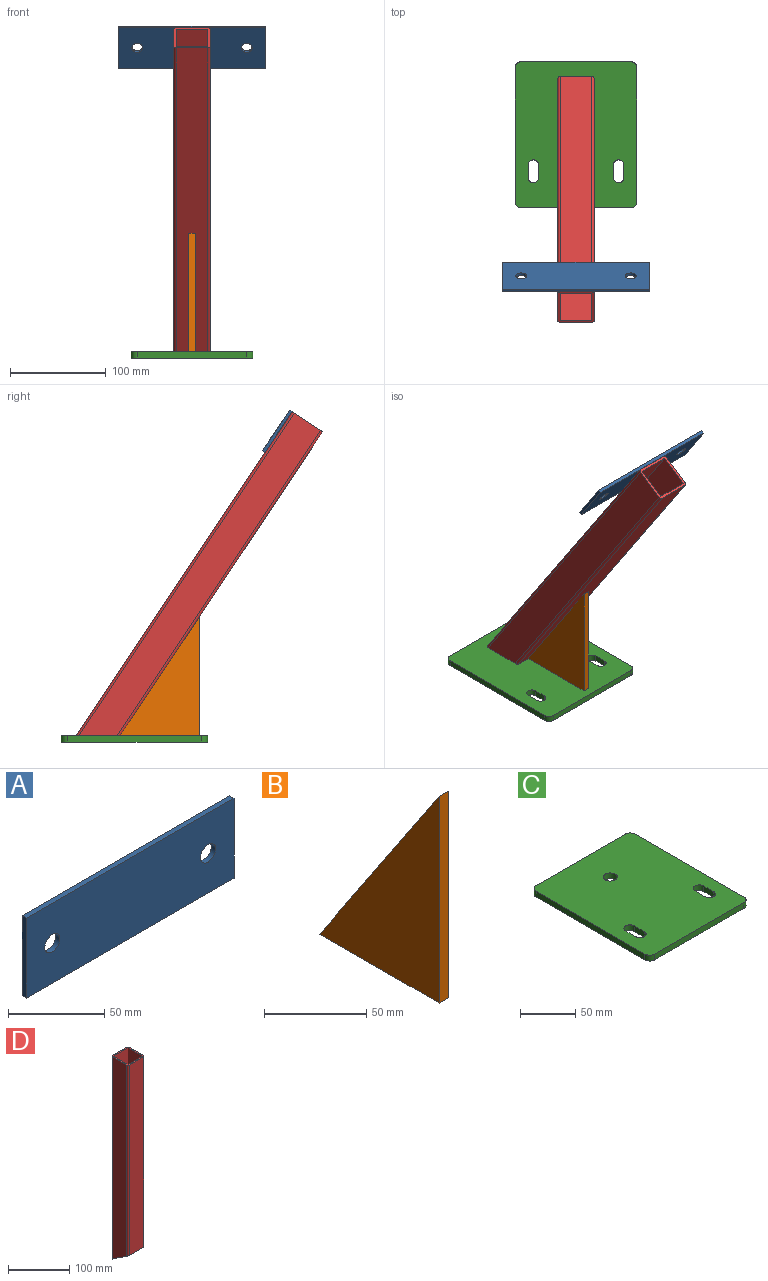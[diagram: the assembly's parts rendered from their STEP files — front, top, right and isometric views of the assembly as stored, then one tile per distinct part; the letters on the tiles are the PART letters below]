
ASSEMBLY  parts=4 mates=3
PART A: 8 faces, bbox 152.4x3.2x50.8 mm
  f0: plane 152.4x50.8mm, normal (0,1,0), area 7547.9mm2, adj f2,f3,f4,f5,f6,f7
  f1: plane 152.4x50.8mm, normal (0,-1,0), area 7547.9mm2, adj f2,f3,f4,f5,f6,f7
  f2: plane 152.4x3.18mm, normal (0,0,1), area 483.9mm2, adj f0,f1,f3,f5
  f3: plane 50.8x3.18mm, normal (-1,0,0), area 161.3mm2, adj f0,f1,f2,f4
  f4: plane 152.4x3.18mm, normal (0,0,-1), area 483.9mm2, adj f0,f1,f3,f5
  f5: plane 50.8x3.18mm, normal (1,0,0), area 161.3mm2, adj f0,f1,f2,f4
  f6: cylinder r=5.56mm len=11.11mm, axis (0,-1,0), area 110.8mm2, adj f0,f1
  f7: cylinder r=5.56mm len=11.11mm, axis (0,-1,0), area 110.8mm2, adj f0,f1
PART B: 5 faces, bbox 6.4x82.6x123.8 mm
  f0: plane 82.55x6.35mm, normal (0,0,-1), area 524.2mm2, adj f1,f2,f3,f4
  f1: plane 123.83x82.55mm, normal (0,0.83,0.55), area 945mm2, adj f0,f2,f3,f4
  f2: plane 123.83x6.35mm, normal (0,-1,0), area 786.3mm2, adj f0,f1,f3,f4
  f3: plane 123.83x82.55mm, normal (1,0,0), area 5110.9mm2, adj f0,f1,f2
  f4: plane 123.83x82.55mm, normal (-1,0,0), area 5110.9mm2, adj f0,f1,f2
PART C: 19 faces, bbox 127x152.4x6.4 mm
  f0: plane 114.3x6.35mm, normal (0,1,0), area 725.8mm2, adj f4,f5,f6,f9
  f1: plane 139.7x6.35mm, normal (-1,0,0), area 887.1mm2, adj f4,f5,f6,f7
  f2: plane 114.3x6.35mm, normal (0,-1,0), area 725.8mm2, adj f4,f5,f7,f8
  f3: plane 139.7x6.35mm, normal (1,0,0), area 887.1mm2, adj f4,f5,f8,f9
  f4: plane 152.4x127mm, normal (0,0,-1), area 18717.3mm2, adj f0,f1,f2,f3,f6,f7,f8,f9
  f5: plane 152.4x127mm, normal (0,0,1), area 18717.3mm2, adj f0,f1,f2,f3,f6,f7,f8,f9
  f6: cylinder r=6.35mm len=6.35mm, axis (0,0,-1), area 63.3mm2, adj f0,f1,f4,f5
  f7: cylinder r=6.35mm len=6.35mm, axis (0,0,1), area 63.3mm2, adj f1,f2,f4,f5
  f8: cylinder r=6.35mm len=6.35mm, axis (0,0,-1), area 63.3mm2, adj f2,f3,f4,f5
  f9: cylinder r=6.35mm len=6.35mm, axis (0,0,1), area 63.3mm2, adj f0,f3,f4,f5
  f10: plane 12.7x6.35mm, normal (-1,0,0), area 80.6mm2, adj f4,f5,f11,f13
  f11: cylinder r=5.56mm len=11.11mm, axis (0,0,1), area 110.8mm2, adj f4,f5,f10,f12
  f12: plane 12.7x6.35mm, normal (1,0,0), area 80.6mm2, adj f4,f5,f11,f13
  f13: cylinder r=5.56mm len=11.11mm, axis (0,0,1), area 110.8mm2, adj f4,f5,f10,f12
  f14: plane 12.7x6.35mm, normal (-1,0,0), area 80.6mm2, adj f4,f5,f15,f17
  f15: cylinder r=5.56mm len=11.11mm, axis (0,0,1), area 110.8mm2, adj f4,f5,f14,f16
  f16: plane 12.7x6.35mm, normal (1,0,0), area 80.6mm2, adj f4,f5,f15,f17
  f17: cylinder r=5.56mm len=11.11mm, axis (0,0,1), area 110.8mm2, adj f4,f5,f14,f16
  f18: cylinder r=6.35mm len=12.7mm, axis (0,0,1), area 253.4mm2, adj f4,f5
PART D: 14 faces, bbox 38.1x38.1x406.4 mm
  f0: plane 404.71x33.02mm, normal (1,0,0), area 13000mm2, adj f8,f9,f12,f13
  f1: plane 404.71x33.02mm, normal (-1,0,0), area 13000mm2, adj f8,f9,f10,f11
  f2: plane 404.71x33.02mm, normal (1,0,0), area 13000mm2, adj f3,f5,f8,f9
  f3: plane 404.71x33.02mm, normal (0,-1,0), area 13363.4mm2, adj f2,f4,f8,f9
  f4: plane 404.71x33.02mm, normal (-1,0,0), area 13000mm2, adj f3,f5,f8,f9
  f5: plane 382.69x33.02mm, normal (0,1,0), area 12636.5mm2, adj f2,f4,f8,f9
  f6: plane 406.4x33.02mm, normal (0,1,0), area 13419.3mm2, adj f8,f9,f10,f13
  f7: plane 381x33.02mm, normal (0,-1,0), area 12580.6mm2, adj f8,f9,f11,f12
  f8: plane 38.1x38.1mm, normal (0,0,1), area 355.8mm2, adj f0,f1,f2,f3,f4,f5,f6,f7
  f9: plane 38.1x38.1mm, normal (0,-0.55,-0.83), area 427.6mm2, adj f0,f1,f2,f3,f4,f5,f6,f7
  f10: cylinder r=2.54mm len=406.4mm, axis (0,0,1), area 1619mm2, adj f1,f6,f8,f9
  f11: cylinder r=2.54mm len=382.69mm, axis (0,0,-1), area 1522.6mm2, adj f1,f7,f8,f9
  f12: cylinder r=2.54mm len=382.69mm, axis (0,0,1), area 1522.6mm2, adj f0,f7,f8,f9
  f13: cylinder r=2.54mm len=406.4mm, axis (0,0,-1), area 1619mm2, adj f0,f6,f8,f9
PLACE A rot(axis=(1,0,0),33.7deg) t=(0,-151.09,317.01)mm
PLACE B t=(0,-0.33,0)mm
PLACE C t=(0,-38.81,0)mm
PLACE D rot(axis=(1,0,0),33.7deg) t=(0,44.4,-10.57)mm
MATE fastened D.f6 <-> A.f1  axis (0,0.83,0.55) through (0,-165.18,338.15)mm
MATE fastened C.f5 <-> D.f9  axis (0,0,1) through (0,75.49,0)mm
MATE fastened D.f7 <-> B.f1  axis (0,-0.83,-0.55) through (0,14.46,0)mm
